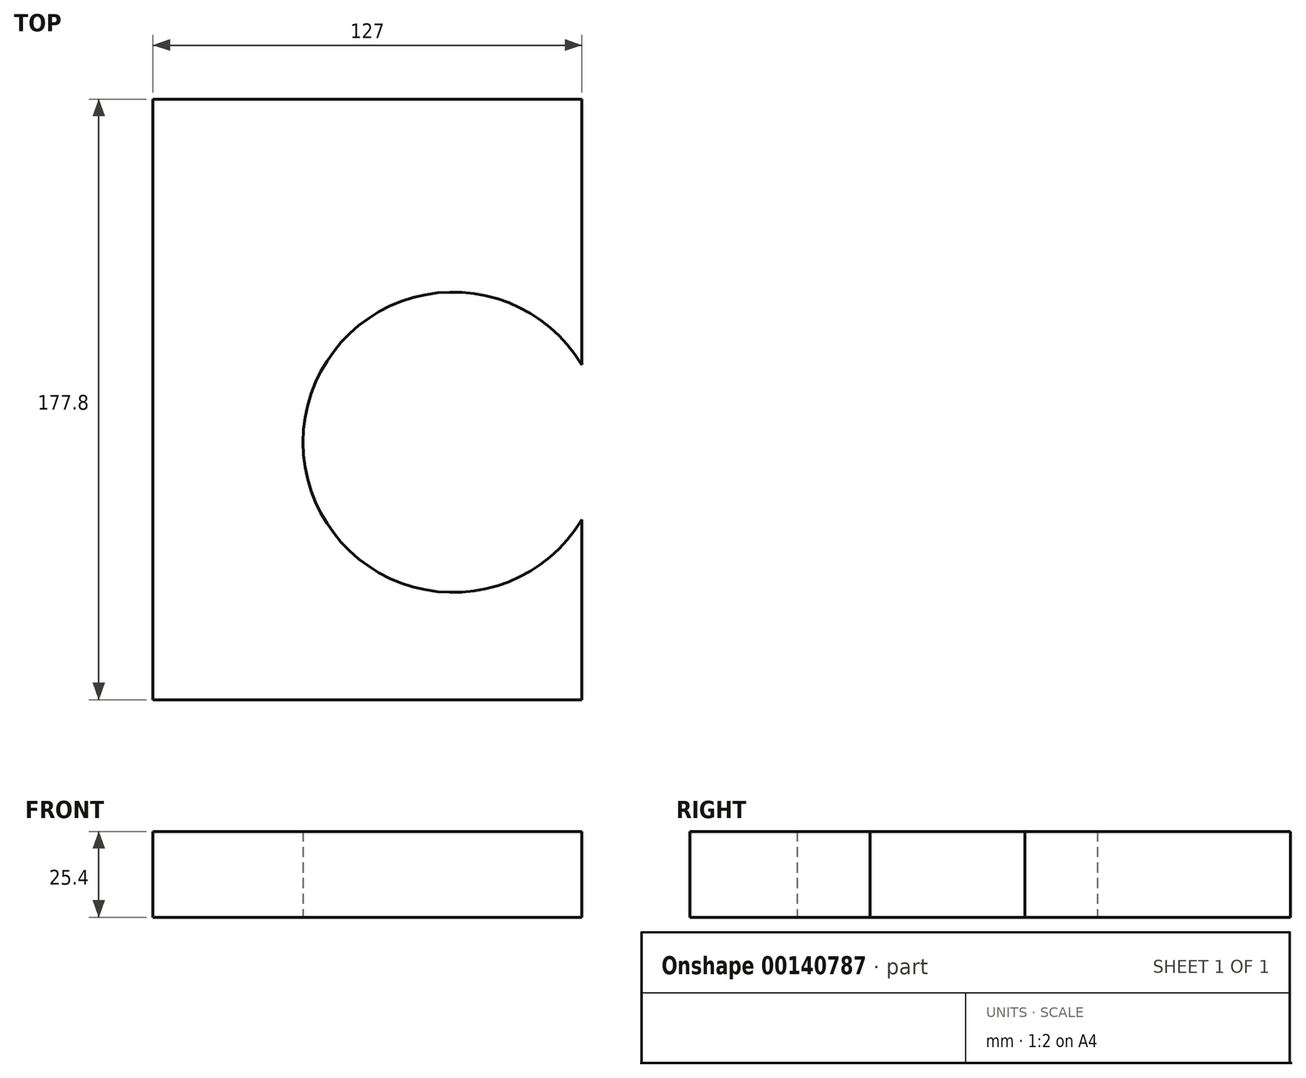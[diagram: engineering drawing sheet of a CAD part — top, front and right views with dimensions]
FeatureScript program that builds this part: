
annotation { "Feature Type Name" : "Feature", "Feature Type Description" : "" }
export const myFeature = defineFeature(function(context is Context, id is Id, definition is map)
    precondition{}
    {
        {
            var Q0;
            Q0=qCreatedBy(makeId("Top.planeOp"),FACE);
            var sketch = newSketch(context, id + "F0", { "sketchPlane" : qUnion([Q0])});
            skLineSegment(sketch, "E0.bottom", {"start": v(-63.5, 88.9) * mm, "end": v(63.5, 88.9) * mm});
            skLineSegment(sketch, "E0.top", {"start": v(-63.5, -88.9) * mm, "end": v(63.5, -88.9) * mm});
            skLineSegment(sketch, "E0.left", {"start": v(-63.5, 88.9) * mm, "end": v(-63.5, -88.9) * mm});
            skLineSegment(sketch, "E0.right", {"start": v(63.5, 88.9) * mm, "end": v(63.5, -88.9) * mm});
            skSolve(sketch);
        }
        {
            var Q0;
            Q0=qCreatedBy(makeId("Top.planeOp"),FACE);
            var sketch = newSketch(context, id + "F1", { "sketchPlane" : qUnion([Q0])});
            skLineSegment(sketch, "E1.0", {"start": v(-63.5, 88.9) * mm, "end": v(63.5, 88.9) * mm});
            skLineSegment(sketch, "E1.1", {"start": v(-63.5, 88.9) * mm, "end": v(-63.5, -88.9) * mm});
            skLineSegment(sketch, "E1.2", {"start": v(63.5, 88.9) * mm, "end": v(63.5, -88.9) * mm});
            skLineSegment(sketch, "E1.3", {"start": v(-63.5, -88.9) * mm, "end": v(63.5, -88.9) * mm});
            skCircle(sketch, "E2", {"center": v(25.4, -12.7) * mm, "radius": 44.45 * mm});
            skSolve(sketch);
        }
        {
            var Q0;
            {var subQ4=sQuery(id+"F1.wireOp",EDGE,"E1.0");Q0=makeQuery(id+"F1.imprint","IMPRINT",FACE,{"disambiguationData":[TD([[makeQuery(id+"F1.imprint","IMPRINT",EDGE,{"derivedFrom":subQ4}),-1.0]])]});}
            var Q1;
            {var subQ0=sQuery(id+"F1.wireOp",EDGE,"E2");var subQ1=sQuery(id+"F1.wireOp",EDGE,"E1.2");var subQ2=makeQuery(id+"F1.imprint","INTERSECT",VERTEX,{"disambiguationData":[OD(0.0)],"derivedFrom":[subQ1,subQ0]});Q1=makeQuery(id+"F1.imprint","IMPRINT",FACE,{"disambiguationData":[TD([[makeQuery(id+"F1.imprint","IMPRINT",EDGE,{"disambiguationData":[TD([[subQ2,-1.0]])],"derivedFrom":subQ1}),-1.0]])]});}
            extrude(context, id + "F2", {"entities" : qUnion([Q0, Q1]), "depth" : 25.4 * mm});
        }
        {
            var Q0;
            {var subQ0=sQuery(id+"F1.wireOp",EDGE,"E2");var subQ1=sQuery(id+"F1.wireOp",EDGE,"E1.2");var subQ2=makeQuery(id+"F1.imprint","INTERSECT",VERTEX,{"disambiguationData":[OD(0.0)],"derivedFrom":[subQ1,subQ0]});Q0=makeQuery(id+"F1.imprint","IMPRINT",FACE,{"disambiguationData":[TD([[makeQuery(id+"F1.imprint","IMPRINT",EDGE,{"disambiguationData":[TD([[subQ2,-1.0]])],"derivedFrom":subQ1}),-1.0]])]});}
            extrude(context, id + "F3", {"entities" : qUnion([Q0]), "operationType" : NewBodyOperationType.REMOVE, "endBound" : BoundingType.THROUGH_ALL, "depth" : 25.4 * mm});
        }
    });
